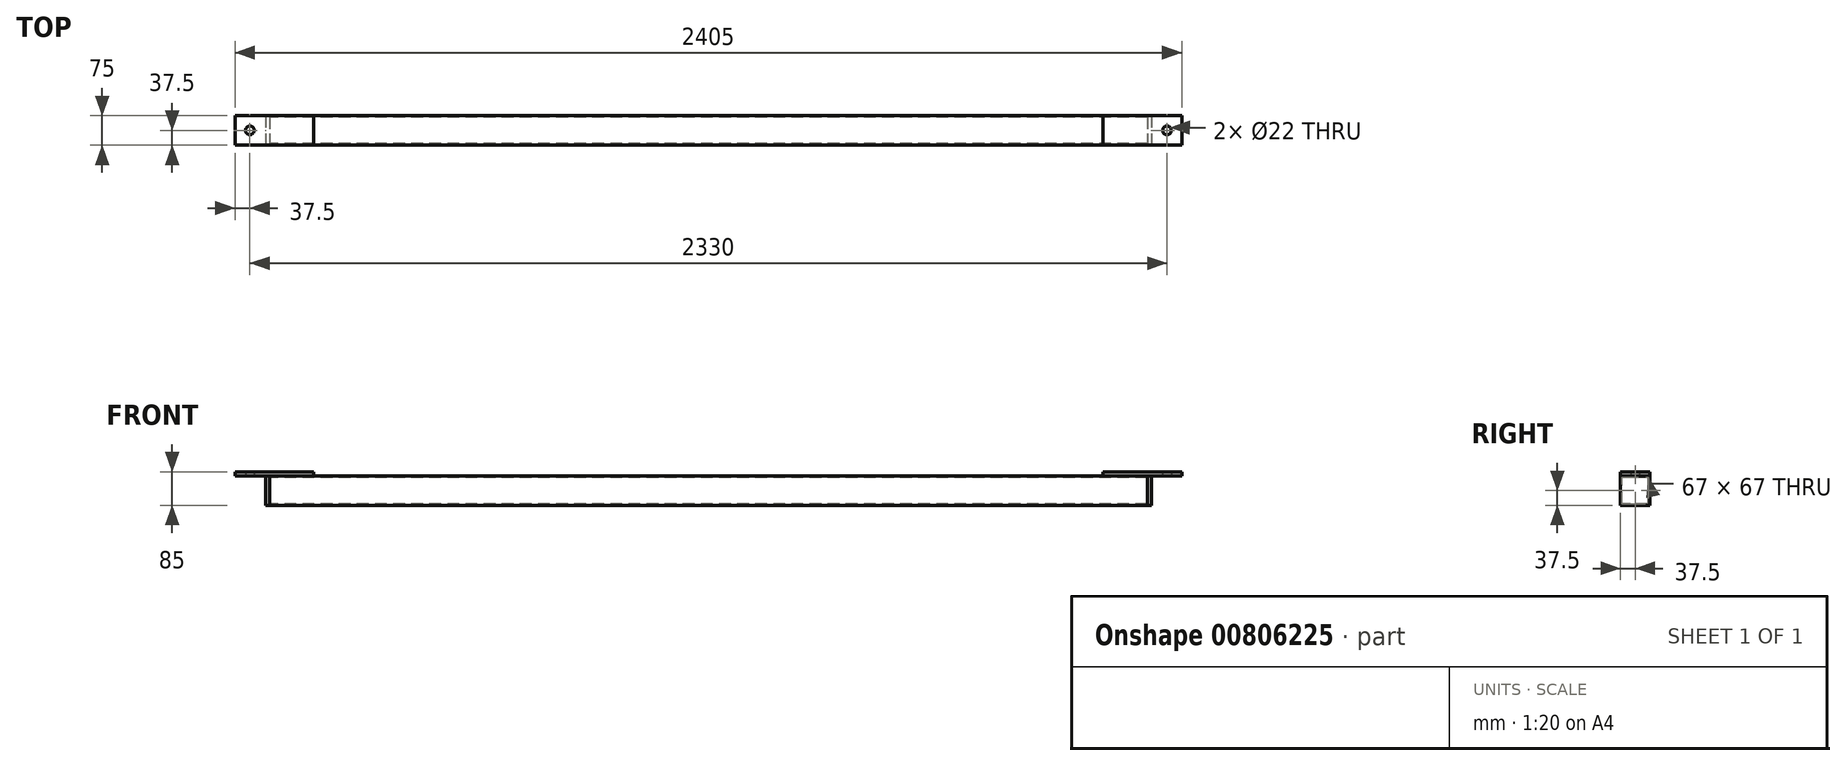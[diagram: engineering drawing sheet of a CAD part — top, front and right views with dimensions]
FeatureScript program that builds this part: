
annotation { "Feature Type Name" : "Feature", "Feature Type Description" : "" }
export const myFeature = defineFeature(function(context is Context, id is Id, definition is map)
    precondition{}
    {
        {
            var Q0;
            Q0=qCreatedBy(makeId("Right.planeOp"),FACE);
            var sketch = newSketch(context, id + "F0", { "sketchPlane" : qUnion([Q0])});
            skLineSegment(sketch, "E0.bottom", {"start": v(37.5, -37.5) * mm, "end": v(-37.5, -37.5) * mm});
            skLineSegment(sketch, "E0.top", {"start": v(37.5, 37.5) * mm, "end": v(-37.5, 37.5) * mm});
            skLineSegment(sketch, "E0.left", {"start": v(37.5, -37.5) * mm, "end": v(37.5, 37.5) * mm});
            skLineSegment(sketch, "E0.right", {"start": v(-37.5, -37.5) * mm, "end": v(-37.5, 37.5) * mm});
            skPoint(sketch, "E0.middle", {"position": v(0, 0) * mm});
            skLineSegment(sketch, "E1.0", {"start": v(-33.5, -33.5) * mm, "end": v(-33.5, 33.5) * mm});
            skLineSegment(sketch, "E1.1", {"start": v(33.5, -33.5) * mm, "end": v(-33.5, -33.5) * mm});
            skLineSegment(sketch, "E1.2", {"start": v(33.5, -33.5) * mm, "end": v(33.5, 33.5) * mm});
            skLineSegment(sketch, "E1.3", {"start": v(33.5, 33.5) * mm, "end": v(-33.5, 33.5) * mm});
            skSolve(sketch);
        }
        {
            var Q0;
            Q0=qSketchRegion(id+"F0",true);
            extrude(context, id + "F1", {"entities" : qUnion([Q0]), "depth" : 2230 * mm, "offsetDistance" : 25 * mm});
        }
        {
            var Q0;
            Q0=makeQuery(id+"F1.opExtrude","CAP_FACE",FACE,{"disambiguationData":[OSD([sQuery(id+"F0.wireOp",EDGE,"E0.bottom"),sQuery(id+"F0.wireOp",EDGE,"E0.top"),sQuery(id+"F0.wireOp",EDGE,"E0.left"),sQuery(id+"F0.wireOp",EDGE,"E0.right"),sQuery(id+"F0.wireOp",EDGE,"E1.0"),sQuery(id+"F0.wireOp",EDGE,"E1.1"),sQuery(id+"F0.wireOp",EDGE,"E1.2"),sQuery(id+"F0.wireOp",EDGE,"E1.3")])],"isStart":false});
            var sketch = newSketch(context, id + "F2", { "sketchPlane" : qUnion([Q0])});
            skLineSegment(sketch, "E2.bottom", {"start": v(37.5, -37.5) * mm, "end": v(-37.5, -37.5) * mm});
            skLineSegment(sketch, "E2.top", {"start": v(37.5, 37.5) * mm, "end": v(-37.5, 37.5) * mm});
            skLineSegment(sketch, "E2.left", {"start": v(37.5, -37.5) * mm, "end": v(37.5, 37.5) * mm});
            skLineSegment(sketch, "E2.right", {"start": v(-37.5, -37.5) * mm, "end": v(-37.5, 37.5) * mm});
            skPoint(sketch, "E2.middle", {"position": v(0, 0) * mm});
            skLineSegment(sketch, "E3.bottom", {"start": v(-37.5, 37.5) * mm, "end": v(37.5, 37.5) * mm});
            skLineSegment(sketch, "E3.top", {"start": v(-37.5, -37.5) * mm, "end": v(37.5, -37.5) * mm});
            skLineSegment(sketch, "E3.left", {"start": v(-37.5, 37.5) * mm, "end": v(-37.5, -37.5) * mm});
            skLineSegment(sketch, "E3.right", {"start": v(37.5, 37.5) * mm, "end": v(37.5, -37.5) * mm});
            skSolve(sketch);
        }
        {
            var Q0;
            Q0=qSketchRegion(id+"F2",true);
            extrude(context, id + "F3", {"entities" : qUnion([Q0]), "depth" : 10 * mm, "offsetDistance" : 25 * mm});
        }
        {
            var Q0;
            Q0=makeQuery(id+"F1.opExtrude","CAP_FACE",FACE,{"disambiguationData":[OSD([sQuery(id+"F0.wireOp",EDGE,"E0.bottom"),sQuery(id+"F0.wireOp",EDGE,"E0.top"),sQuery(id+"F0.wireOp",EDGE,"E0.left"),sQuery(id+"F0.wireOp",EDGE,"E0.right"),sQuery(id+"F0.wireOp",EDGE,"E1.0"),sQuery(id+"F0.wireOp",EDGE,"E1.1"),sQuery(id+"F0.wireOp",EDGE,"E1.2"),sQuery(id+"F0.wireOp",EDGE,"E1.3")])],"isStart":true});
            var sketch = newSketch(context, id + "F4", { "sketchPlane" : qUnion([Q0])});
            skLineSegment(sketch, "E4.bottom", {"start": v(-37.5, -37.5) * mm, "end": v(37.5, -37.5) * mm});
            skLineSegment(sketch, "E4.top", {"start": v(-37.5, 37.5) * mm, "end": v(37.5, 37.5) * mm});
            skLineSegment(sketch, "E4.left", {"start": v(-37.5, -37.5) * mm, "end": v(-37.5, 37.5) * mm});
            skLineSegment(sketch, "E4.right", {"start": v(37.5, -37.5) * mm, "end": v(37.5, 37.5) * mm});
            skSolve(sketch);
        }
        {
            var Q0;
            Q0=qSketchRegion(id+"F4",true);
            extrude(context, id + "F5", {"entities" : qUnion([Q0]), "depth" : 10 * mm, "offsetDistance" : 25 * mm});
        }
        {
            var Q0;
            Q0=makeQuery(id+"F1.opExtrude","SWEPT_FACE",FACE,{"disambiguationData":[OSD([sQuery(id+"F0.wireOp",EDGE,"E0.top")])]});
            var sketch = newSketch(context, id + "F6", { "sketchPlane" : qUnion([Q0])});
            skLineSegment(sketch, "E5", {"start": v(0, 0) * mm, "end": v(-50, 0) * mm});
            skCircle(sketch, "E6", {"center": v(-50, 0) * mm, "radius": 11 * mm});
            skLineSegment(sketch, "E7", {"start": v(0, -37.5) * mm, "end": v(-87.5, -37.5) * mm});
            skLineSegment(sketch, "E8", {"start": v(-87.5, -37.5) * mm, "end": v(-87.5, 37.5) * mm});
            skLineSegment(sketch, "E9", {"start": v(-87.5, 37.5) * mm, "end": v(112.5, 37.5) * mm});
            skLineSegment(sketch, "E10", {"start": v(112.5, 37.5) * mm, "end": v(112.5, -37.5) * mm});
            skLineSegment(sketch, "E11", {"start": v(112.5, -37.5) * mm, "end": v(0, -37.5) * mm});
            skSolve(sketch);
        }
        {
            var Q0;
            Q0=makeQuery(id+"F6.imprint","IMPRINT",FACE,{"disambiguationData":[TD([[makeQuery(id+"F6.imprint","IMPRINT",EDGE,{"derivedFrom":sQuery(id+"F6.wireOp",EDGE,"E6")}),-1.0]])]});
            var Q1;
            {var subQ6=sQuery(id+"F6.wireOp",EDGE,"E10");Q1=makeQuery(id+"F6.imprint","IMPRINT",FACE,{"disambiguationData":[TD([[makeQuery(id+"F6.imprint","IMPRINT",EDGE,{"derivedFrom":subQ6}),-1.0]])]});}
            extrude(context, id + "F7", {"entities" : qUnion([Q0, Q1]), "depth" : 10 * mm, "offsetDistance" : 25 * mm});
        }
        {
            var Q0;
            Q0=makeQuery(id+"F1.opExtrude","SWEPT_FACE",FACE,{"disambiguationData":[OSD([sQuery(id+"F0.wireOp",EDGE,"E0.top")])]});
            var sketch = newSketch(context, id + "F8", { "sketchPlane" : qUnion([Q0])});
            skLineSegment(sketch, "E12", {"start": v(2230, -37.5) * mm, "end": v(2317.5, -37.5) * mm});
            skLineSegment(sketch, "E13", {"start": v(2317.5, -37.5) * mm, "end": v(2317.5, 37.5) * mm});
            skLineSegment(sketch, "E14", {"start": v(2317.5, 37.5) * mm, "end": v(2117.5, 37.5) * mm});
            skLineSegment(sketch, "E15", {"start": v(2117.5, 37.5) * mm, "end": v(2117.5, -37.5) * mm});
            skLineSegment(sketch, "E16", {"start": v(2117.5, -37.5) * mm, "end": v(2230, -37.5) * mm});
            skLineSegment(sketch, "E17", {"start": v(2230, 0) * mm, "end": v(2280, 0) * mm});
            skCircle(sketch, "E18", {"center": v(2280, 0) * mm, "radius": 11 * mm});
            skSolve(sketch);
        }
        {
            var Q0;
            Q0=qSketchRegion(id+"F8",true);
            extrude(context, id + "F9", {"entities" : qUnion([Q0]), "depth" : 10 * mm, "offsetDistance" : 25 * mm});
        }
    });
